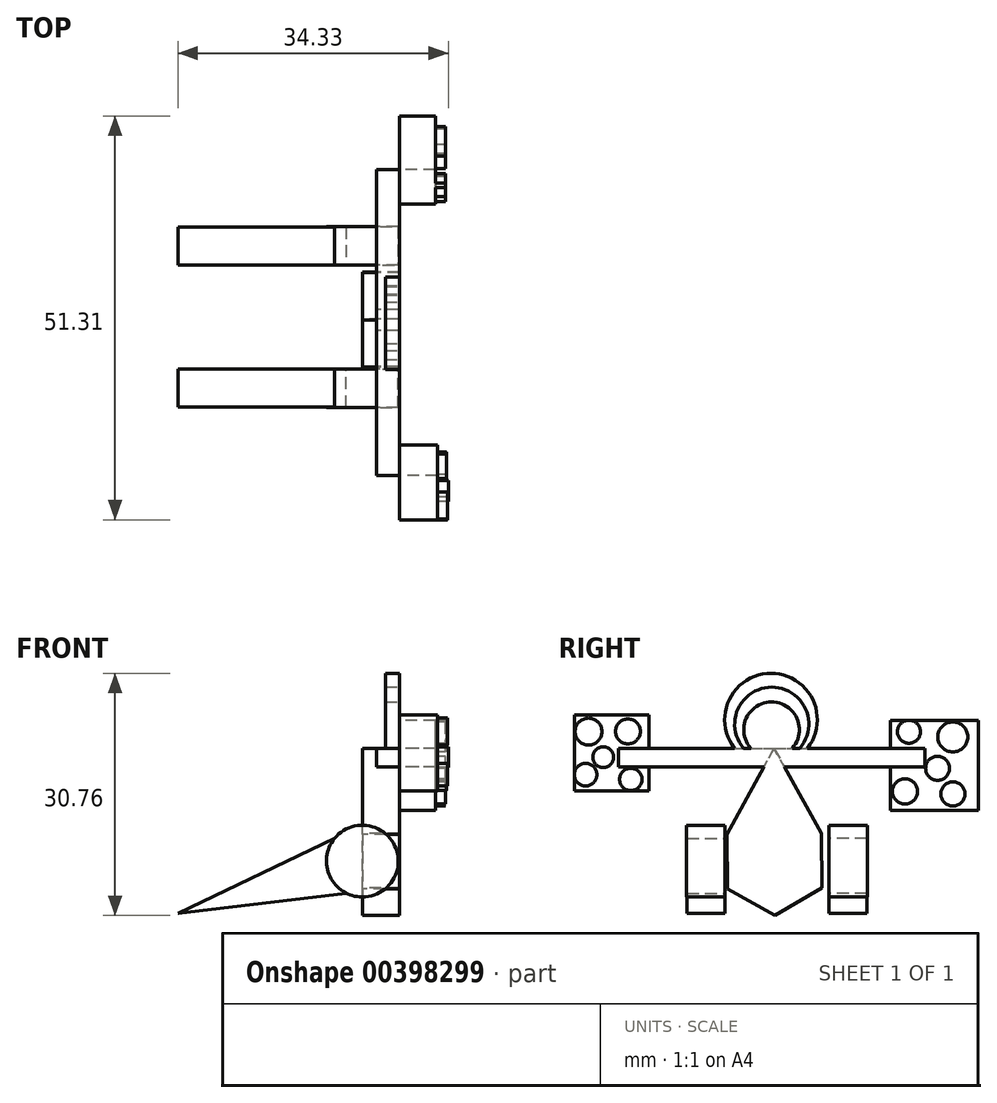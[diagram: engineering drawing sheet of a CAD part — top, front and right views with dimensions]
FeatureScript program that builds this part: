
annotation { "Feature Type Name" : "Feature", "Feature Type Description" : "" }
export const myFeature = defineFeature(function(context is Context, id is Id, definition is map)
    precondition{}
    {
        {
            var Q0;
            Q0=qCreatedBy(makeId("Front.planeOp"),FACE);
            var sketch = newSketch(context, id + "F0", { "sketchPlane" : qUnion([Q0])});
            skCircle(sketch, "E0", {"center": v(0, 0) * mm, "radius": 91.11 * mm});
            skSolve(sketch);
        }
        {
            var Q0;
            Q0=makeQuery(id+"F0.imprint","IMPRINT",FACE,{"disambiguationData":[TD([[makeQuery(id+"F0.imprint","IMPRINT",EDGE,{"derivedFrom":sQuery(id+"F0.wireOp",EDGE,"E0")}),1.0]])]});
            extrude(context, id + "F1", {"entities" : qUnion([Q0]), "depth" : 98.04 * mm});
        }
        {
            var Q0;
            Q0=makeQuery(id+"F1.opExtrude","CAP_FACE",FACE,{"disambiguationData":[OSD([sQuery(id+"F0.wireOp",EDGE,"E0")])],"isStart":true});
            var sketch = newSketch(context, id + "F2", { "sketchPlane" : qUnion([Q0])});
            skLineSegment(sketch, "E1", {"start": v(0, 91.11) * mm, "end": v(-434.23, -92.92) * mm});
            skLineSegment(sketch, "E2", {"start": v(0, -76.65) * mm, "end": v(-434.23, -92.92) * mm});
            skLineSegment(sketch, "E3", {"start": v(0, 91.11) * mm, "end": v(468.1, -132.24) * mm});
            skLineSegment(sketch, "E4", {"start": v(468.1, -132.24) * mm, "end": v(0, -76.65) * mm});
            skSolve(sketch);
        }
        {
            var Q0;
            {var subQ0=sQuery(id+"F2.wireOp",EDGE,"E4");var subQ1=sQuery(id+"F2.wireOp",EDGE,"E3");var subQ2=makeQuery(id+"F2.imprint","INTERSECT",VERTEX,{"derivedFrom":[subQ1,subQ0]});Q0=makeQuery(id+"F2.imprint","IMPRINT",FACE,{"disambiguationData":[TD([[makeQuery(id+"F2.imprint","IMPRINT",EDGE,{"disambiguationData":[TD([[subQ2,1.0]])],"derivedFrom":subQ1}),-1.0]])]});}
            extrude(context, id + "F3", {"entities" : qUnion([Q0]), "operationType" : NewBodyOperationType.ADD, "oppositeDirection" : true, "depth" : 96.52 * mm});
        }
        {
            var Q0;
            Q0=makeQuery(id+"F1.opExtrude","SWEPT_BODY",BODY,{"disambiguationData":[OSD([sQuery(id+"F0.wireOp",EDGE,"E0")])]});
            var Q1;
            Q1=qCreatedBy(makeId("Front.planeOp"),FACE);
            mirror(context, id + "F4", {"entities" : qUnion([Q0]), "mirrorPlane" : qUnion([Q1])});
        }
        {
            var Q0;
            Q0=makeQuery(id+"F4.opPattern","COPY",BODY,{"derivedFrom":makeQuery(id+"F1.opExtrude","SWEPT_BODY",BODY,{"disambiguationData":[OSD([sQuery(id+"F0.wireOp",EDGE,"E0")])]}),"instanceName":"1"});
            transform(context, id + "F5", {"entities" : qUnion([Q0]), "transformType" : TransformType.TRANSLATION_3D, "dx" : 0 * mm, "dy" : 264.16 * mm, "dz" : 0 * mm, "makeCopy" : false});
        }
        {
            var Q0;
            Q0=qCreatedBy(makeId("Right.planeOp"),FACE);
            var sketch = newSketch(context, id + "F6", { "sketchPlane" : qUnion([Q0])});
            skCircle(sketch, "E5.cCircle", {"center": v(125.72, 0) * mm, "radius": 119.75 * mm, "construction": true});
            skLineSegment(sketch, "E5.0", {"start": v(5.37, 68.07) * mm, "end": v(124.5, 138.26) * mm});
            skLineSegment(sketch, "E5.1", {"start": v(124.5, 138.26) * mm, "end": v(244.85, 70.2) * mm});
            skLineSegment(sketch, "E5.2", {"start": v(244.85, 70.2) * mm, "end": v(246.08, -68.07) * mm});
            skLineSegment(sketch, "E5.3", {"start": v(246.08, -68.07) * mm, "end": v(126.95, -138.26) * mm});
            skLineSegment(sketch, "E5.4", {"start": v(126.95, -138.26) * mm, "end": v(6.6, -70.2) * mm});
            skLineSegment(sketch, "E5.5", {"start": v(6.6, -70.2) * mm, "end": v(5.37, 68.07) * mm});
            skPoint(sketch, "E5.0.midPoint", {"position": v(64.93, 103.17) * mm});
            skSolve(sketch);
        }
        {
            var Q0;
            Q0=makeQuery(id+"F6.imprint","IMPRINT",FACE,{"disambiguationData":[TD([[makeQuery(id+"F6.imprint","IMPRINT",EDGE,{"derivedFrom":sQuery(id+"F6.wireOp",EDGE,"E5.0")}),-1.0]])]});
            extrude(context, id + "F7", {"entities" : qUnion([Q0]), "depth" : 93.98 * mm});
        }
        {
            var Q0;
            Q0=makeQuery(id+"F7.opExtrude","CAP_FACE",FACE,{"disambiguationData":[OSD([sQuery(id+"F6.wireOp",EDGE,"E5.0"),sQuery(id+"F6.wireOp",EDGE,"E5.1"),sQuery(id+"F6.wireOp",EDGE,"E5.2"),sQuery(id+"F6.wireOp",EDGE,"E5.3"),sQuery(id+"F6.wireOp",EDGE,"E5.4"),sQuery(id+"F6.wireOp",EDGE,"E5.5")])],"isStart":false});
            var sketch = newSketch(context, id + "F8", { "sketchPlane" : qUnion([Q0])});
            skLineSegment(sketch, "E6", {"start": v(5.37, 68.07) * mm, "end": v(124.5, 286.89) * mm});
            skLineSegment(sketch, "E7", {"start": v(244.85, 70.2) * mm, "end": v(124.5, 286.89) * mm});
            skSolve(sketch);
        }
        {
            var Q0;
            Q0=makeQuery(id+"F8.imprint","IMPRINT",FACE,{"disambiguationData":[TD([[makeQuery(id+"F8.imprint","IMPRINT",EDGE,{"derivedFrom":sQuery(id+"F8.wireOp",EDGE,"E6")}),-1.0]])]});
            extrude(context, id + "F9", {"entities" : qUnion([Q0]), "operationType" : NewBodyOperationType.ADD, "oppositeDirection" : true, "depth" : 93.98 * mm});
        }
        {
            var Q0;
            {var subQ0=sQuery(id+"F6.wireOp",EDGE,"E5.1");var subQ1=sQuery(id+"F6.wireOp",EDGE,"E5.0");Q0=makeQuery(id+"F9.boolean.opBoolean","MERGE",FACE,{"derivedFrom":[makeQuery(id+"F7.opExtrude","CAP_FACE",FACE,{"disambiguationData":[OSD([subQ1,subQ0,sQuery(id+"F6.wireOp",EDGE,"E5.2"),sQuery(id+"F6.wireOp",EDGE,"E5.3"),sQuery(id+"F6.wireOp",EDGE,"E5.4"),sQuery(id+"F6.wireOp",EDGE,"E5.5")])],"isStart":false}),makeQuery(id+"F9.opExtrude","CAP_FACE",FACE,{"disambiguationData":[OSD([subQ1,subQ0,sQuery(id+"F8.wireOp",EDGE,"E6"),sQuery(id+"F8.wireOp",EDGE,"E7")])],"isStart":true})]});}
            var sketch = newSketch(context, id + "F10", { "sketchPlane" : qUnion([Q0])});
            skLineSegment(sketch, "E8.bottom", {"start": v(-270.15, 286.89) * mm, "end": v(507.6, 286.89) * mm});
            skLineSegment(sketch, "E8.top", {"start": v(-270.15, 238.84) * mm, "end": v(507.6, 238.84) * mm});
            skLineSegment(sketch, "E8.left", {"start": v(-270.15, 286.89) * mm, "end": v(-270.15, 238.84) * mm});
            skLineSegment(sketch, "E8.right", {"start": v(507.6, 286.89) * mm, "end": v(507.6, 238.84) * mm});
            skSolve(sketch);
        }
        {
            var Q0;
            Q0 = qSketchRegion(id + "F10", true);
            extrude(context, id + "F11", {"entities" : qUnion([Q0]), "operationType" : NewBodyOperationType.ADD, "oppositeDirection" : true, "depth" : 58.42 * mm});
        }
        {
            var Q0;
            {var subQ0=sQuery(id+"F6.wireOp",EDGE,"E5.1");var subQ1=sQuery(id+"F6.wireOp",EDGE,"E5.0");Q0=makeQuery(id+"F11.boolean.opBoolean","MERGE",FACE,{"derivedFrom":[makeQuery(id+"F9.boolean.opBoolean","MERGE",FACE,{"derivedFrom":[makeQuery(id+"F7.opExtrude","CAP_FACE",FACE,{"disambiguationData":[OSD([subQ1,subQ0,sQuery(id+"F6.wireOp",EDGE,"E5.2"),sQuery(id+"F6.wireOp",EDGE,"E5.3"),sQuery(id+"F6.wireOp",EDGE,"E5.4"),sQuery(id+"F6.wireOp",EDGE,"E5.5")])],"isStart":false}),makeQuery(id+"F9.opExtrude","CAP_FACE",FACE,{"disambiguationData":[OSD([subQ1,subQ0,sQuery(id+"F8.wireOp",EDGE,"E6"),sQuery(id+"F8.wireOp",EDGE,"E7")])],"isStart":true})]}),makeQuery(id+"F11.opExtrude","CAP_FACE",FACE,{"disambiguationData":[OSD([sQuery(id+"F10.wireOp",EDGE,"E8.bottom"),sQuery(id+"F10.wireOp",EDGE,"E8.top"),sQuery(id+"F10.wireOp",EDGE,"E8.left"),sQuery(id+"F10.wireOp",EDGE,"E8.right")])],"isStart":true})]});}
            var sketch = newSketch(context, id + "F12", { "sketchPlane" : qUnion([Q0])});
            skLineSegment(sketch, "E9.bottom", {"start": v(-383, 179.03) * mm, "end": v(-193.33, 179.03) * mm});
            skLineSegment(sketch, "E9.top", {"start": v(-383, 371.33) * mm, "end": v(-193.33, 371.33) * mm});
            skLineSegment(sketch, "E9.left", {"start": v(-383, 179.03) * mm, "end": v(-383, 371.33) * mm});
            skLineSegment(sketch, "E9.right", {"start": v(-193.33, 179.03) * mm, "end": v(-193.33, 371.33) * mm});
            skSolve(sketch);
        }
        {
            var Q0;
            {var subQ1=sQuery(id+"F12.wireOp",EDGE,"E9.bottom");Q0=makeQuery(id+"F12.imprint","IMPRINT",FACE,{"disambiguationData":[TD([[makeQuery(id+"F12.imprint","IMPRINT",EDGE,{"derivedFrom":subQ1}),1.0]])]});}
            extrude(context, id + "F13", {"entities" : qUnion([Q0]), "depth" : 96.52 * mm});
        }
        {
            var Q0;
            {var subQ0=sQuery(id+"F6.wireOp",EDGE,"E5.1");var subQ1=sQuery(id+"F6.wireOp",EDGE,"E5.0");Q0=makeQuery(id+"F11.boolean.opBoolean","MERGE",FACE,{"derivedFrom":[makeQuery(id+"F9.boolean.opBoolean","MERGE",FACE,{"derivedFrom":[makeQuery(id+"F7.opExtrude","CAP_FACE",FACE,{"disambiguationData":[OSD([subQ1,subQ0,sQuery(id+"F6.wireOp",EDGE,"E5.2"),sQuery(id+"F6.wireOp",EDGE,"E5.3"),sQuery(id+"F6.wireOp",EDGE,"E5.4"),sQuery(id+"F6.wireOp",EDGE,"E5.5")])],"isStart":false}),makeQuery(id+"F9.opExtrude","CAP_FACE",FACE,{"disambiguationData":[OSD([subQ1,subQ0,sQuery(id+"F8.wireOp",EDGE,"E6"),sQuery(id+"F8.wireOp",EDGE,"E7")])],"isStart":true})]}),makeQuery(id+"F11.opExtrude","CAP_FACE",FACE,{"disambiguationData":[OSD([sQuery(id+"F10.wireOp",EDGE,"E8.bottom"),sQuery(id+"F10.wireOp",EDGE,"E8.top"),sQuery(id+"F10.wireOp",EDGE,"E8.left"),sQuery(id+"F10.wireOp",EDGE,"E8.right")])],"isStart":true})]});}
            var sketch = newSketch(context, id + "F14", { "sketchPlane" : qUnion([Q0])});
            skLineSegment(sketch, "E10.bottom", {"start": v(643.3, 129.12) * mm, "end": v(420.02, 129.12) * mm});
            skLineSegment(sketch, "E10.top", {"start": v(643.3, 357.33) * mm, "end": v(420.02, 357.33) * mm});
            skLineSegment(sketch, "E10.left", {"start": v(643.3, 129.12) * mm, "end": v(643.3, 357.33) * mm});
            skLineSegment(sketch, "E10.right", {"start": v(420.02, 129.12) * mm, "end": v(420.02, 357.33) * mm});
            skSolve(sketch);
        }
        {
            var Q0;
            {var subQ1=sQuery(id+"F14.wireOp",EDGE,"E10.bottom");Q0=makeQuery(id+"F14.imprint","IMPRINT",FACE,{"disambiguationData":[TD([[makeQuery(id+"F14.imprint","IMPRINT",EDGE,{"derivedFrom":subQ1}),-1.0]])]});}
            extrude(context, id + "F15", {"entities" : qUnion([Q0]), "depth" : 91.44 * mm});
        }
        {
            var Q0;
            Q0=makeQuery(id+"F13.opExtrude","CAP_FACE",FACE,{"disambiguationData":[OSD([sQuery(id+"F10.wireOp",EDGE,"E8.bottom"),sQuery(id+"F10.wireOp",EDGE,"E8.top"),sQuery(id+"F10.wireOp",EDGE,"E8.left"),sQuery(id+"F12.wireOp",EDGE,"E9.bottom"),sQuery(id+"F12.wireOp",EDGE,"E9.top"),sQuery(id+"F12.wireOp",EDGE,"E9.left"),sQuery(id+"F12.wireOp",EDGE,"E9.right")])],"isStart":false});
            var sketch = newSketch(context, id + "F16", { "sketchPlane" : qUnion([Q0])});
            skCircle(sketch, "E11", {"center": v(-239.34, 329.1) * mm, "radius": 32.95 * mm});
            skPoint(sketch, "E11.centerSnap0", {"position": v(-193.33, 329.1) * mm});
            skCircle(sketch, "E12", {"center": v(-346.66, 329.1) * mm, "radius": 34.15 * mm});
            skCircle(sketch, "E13", {"center": v(-354.15, 219.75) * mm, "radius": 28.7 * mm});
            skCircle(sketch, "E14", {"center": v(-239.34, 207.67) * mm, "radius": 28.52 * mm});
            skCircle(sketch, "E15", {"center": v(-309.5, 263.98) * mm, "radius": 26.29 * mm});
            skSolve(sketch);
        }
        {
            var Q0;
            Q0=makeQuery(id+"F16.imprint","IMPRINT",FACE,{"disambiguationData":[TD([[makeQuery(id+"F16.imprint","IMPRINT",EDGE,{"derivedFrom":sQuery(id+"F16.wireOp",EDGE,"E12")}),1.0]])]});
            var Q1;
            Q1=sQuery(id+"F16.wireOp",EDGE,"E12");
            extrude(context, id + "F17", {"entities" : qUnion([Q0]), "operationType" : NewBodyOperationType.ADD, "surfaceEntities" : qUnion([Q1]), "depth" : 25.4 * mm});
        }
        {
            var Q0;
            Q0=makeQuery(id+"F13.opExtrude","CAP_FACE",FACE,{"disambiguationData":[OSD([sQuery(id+"F10.wireOp",EDGE,"E8.bottom"),sQuery(id+"F10.wireOp",EDGE,"E8.top"),sQuery(id+"F10.wireOp",EDGE,"E8.left"),sQuery(id+"F12.wireOp",EDGE,"E9.bottom"),sQuery(id+"F12.wireOp",EDGE,"E9.top"),sQuery(id+"F12.wireOp",EDGE,"E9.left"),sQuery(id+"F12.wireOp",EDGE,"E9.right")])],"isStart":false});
            var sketch = newSketch(context, id + "F18", { "sketchPlane" : qUnion([Q0])});
            skCircle(sketch, "E16", {"center": v(-246.53, 329.52) * mm, "radius": 31.43 * mm});
            skSolve(sketch);
        }
        {
            var Q0;
            Q0=makeQuery(id+"F18.imprint","IMPRINT",FACE,{"disambiguationData":[TD([[makeQuery(id+"F18.imprint","IMPRINT",EDGE,{"derivedFrom":sQuery(id+"F18.wireOp",EDGE,"E16")}),1.0]])]});
            var Q1;
            Q1=sQuery(id+"F18.wireOp",EDGE,"E16");
            extrude(context, id + "F19", {"entities" : qUnion([Q0]), "operationType" : NewBodyOperationType.ADD, "surfaceEntities" : qUnion([Q1]), "endBound" : BoundingType.SYMMETRIC, "depth" : 45.72 * mm});
        }
        {
            var Q0;
            Q0=makeQuery(id+"F16.imprint","IMPRINT",FACE,{"disambiguationData":[TD([[makeQuery(id+"F16.imprint","IMPRINT",EDGE,{"derivedFrom":sQuery(id+"F16.wireOp",EDGE,"E15")}),1.0]])]});
            var Q1;
            Q1=sQuery(id+"F16.wireOp",EDGE,"E15");
            extrude(context, id + "F20", {"entities" : qUnion([Q0]), "operationType" : NewBodyOperationType.ADD, "surfaceEntities" : qUnion([Q1]), "depth" : 27.94 * mm});
        }
        {
            var Q0;
            Q0=makeQuery(id+"F16.imprint","IMPRINT",FACE,{"disambiguationData":[TD([[makeQuery(id+"F16.imprint","IMPRINT",EDGE,{"derivedFrom":sQuery(id+"F16.wireOp",EDGE,"E13")}),1.0]])]});
            var Q1;
            Q1=sQuery(id+"F16.wireOp",EDGE,"E13");
            extrude(context, id + "F21", {"entities" : qUnion([Q0]), "operationType" : NewBodyOperationType.ADD, "surfaceEntities" : qUnion([Q1]), "depth" : 25.4 * mm});
        }
        {
            var Q0;
            Q0=makeQuery(id+"F16.imprint","IMPRINT",FACE,{"disambiguationData":[TD([[makeQuery(id+"F16.imprint","IMPRINT",EDGE,{"derivedFrom":sQuery(id+"F16.wireOp",EDGE,"E14")}),1.0]])]});
            var Q1;
            Q1=sQuery(id+"F16.wireOp",EDGE,"E14");
            extrude(context, id + "F22", {"entities" : qUnion([Q0]), "operationType" : NewBodyOperationType.ADD, "surfaceEntities" : qUnion([Q1]), "depth" : 22.86 * mm});
        }
        {
            var Q0;
            Q0=makeQuery(id+"F15.opExtrude","CAP_FACE",FACE,{"disambiguationData":[OSD([sQuery(id+"F10.wireOp",EDGE,"E8.bottom"),sQuery(id+"F10.wireOp",EDGE,"E8.top"),sQuery(id+"F10.wireOp",EDGE,"E8.right"),sQuery(id+"F14.wireOp",EDGE,"E10.bottom"),sQuery(id+"F14.wireOp",EDGE,"E10.top"),sQuery(id+"F14.wireOp",EDGE,"E10.left"),sQuery(id+"F14.wireOp",EDGE,"E10.right")])],"isStart":false});
            var sketch = newSketch(context, id + "F23", { "sketchPlane" : qUnion([Q0])});
            skCircle(sketch, "E17", {"center": v(578.72, 315.62) * mm, "radius": 38.04 * mm});
            skCircle(sketch, "E18", {"center": v(457.24, 177.07) * mm, "radius": 32 * mm});
            skCircle(sketch, "E19", {"center": v(579.03, 170.7) * mm, "radius": 30.77 * mm});
            skCircle(sketch, "E20", {"center": v(467.35, 328.58) * mm, "radius": 29.36 * mm});
            skCircle(sketch, "E21", {"center": v(540.02, 235.78) * mm, "radius": 30.37 * mm});
            skSolve(sketch);
        }
        {
            var Q0;
            {var subQ0=sQuery(id+"F23.wireOp",EDGE,"E20");var subQ1=makeQuery(id+"F15.opExtrude","CAP_EDGE",EDGE,{"disambiguationData":[OSD([sQuery(id+"F14.wireOp",EDGE,"E10.top")])],"isStart":false});var subQ2=makeQuery(id+"F23.imprint","INTERSECT",VERTEX,{"disambiguationData":[OD(0.0)],"derivedFrom":[subQ1,subQ0]});Q0=makeQuery(id+"F23.imprint","IMPRINT",FACE,{"disambiguationData":[TD([[makeQuery(id+"F23.imprint","IMPRINT",EDGE,{"disambiguationData":[TD([[subQ2,1.0]])],"derivedFrom":subQ0}),1.0]])]});}
            var Q1;
            Q1=sQuery(id+"F23.wireOp",EDGE,"E20");
            extrude(context, id + "F24", {"entities" : qUnion([Q0]), "operationType" : NewBodyOperationType.ADD, "surfaceEntities" : qUnion([Q1]), "depth" : 25.4 * mm});
        }
        {
            var Q0;
            Q0=makeQuery(id+"F23.imprint","IMPRINT",FACE,{"disambiguationData":[TD([[makeQuery(id+"F23.imprint","IMPRINT",EDGE,{"derivedFrom":sQuery(id+"F23.wireOp",EDGE,"E17")}),1.0]])]});
            var Q1;
            Q1=sQuery(id+"F23.wireOp",EDGE,"E17");
            extrude(context, id + "F25", {"entities" : qUnion([Q0]), "operationType" : NewBodyOperationType.ADD, "surfaceEntities" : qUnion([Q1]), "depth" : 25.4 * mm});
        }
        {
            var Q0;
            Q0=makeQuery(id+"F23.imprint","IMPRINT",FACE,{"disambiguationData":[TD([[makeQuery(id+"F23.imprint","IMPRINT",EDGE,{"derivedFrom":sQuery(id+"F23.wireOp",EDGE,"E21")}),1.0]])]});
            var Q1;
            Q1=sQuery(id+"F23.wireOp",EDGE,"E21");
            extrude(context, id + "F26", {"entities" : qUnion([Q0]), "operationType" : NewBodyOperationType.ADD, "surfaceEntities" : qUnion([Q1]), "depth" : 25.4 * mm});
        }
        {
            var Q0;
            Q0=makeQuery(id+"F23.imprint","IMPRINT",FACE,{"disambiguationData":[TD([[makeQuery(id+"F23.imprint","IMPRINT",EDGE,{"derivedFrom":sQuery(id+"F23.wireOp",EDGE,"E18")}),1.0]])]});
            var Q1;
            Q1=sQuery(id+"F23.wireOp",EDGE,"E18");
            extrude(context, id + "F27", {"entities" : qUnion([Q0]), "operationType" : NewBodyOperationType.ADD, "surfaceEntities" : qUnion([Q1]), "depth" : 25.4 * mm});
        }
        {
            var Q0;
            Q0=makeQuery(id+"F23.imprint","IMPRINT",FACE,{"disambiguationData":[TD([[makeQuery(id+"F23.imprint","IMPRINT",EDGE,{"derivedFrom":sQuery(id+"F23.wireOp",EDGE,"E19")}),1.0]])]});
            extrude(context, id + "F28", {"entities" : qUnion([Q0]), "operationType" : NewBodyOperationType.ADD, "depth" : 25.4 * mm});
        }
        {
            var Q0;
            {var subQ0=sQuery(id+"F6.wireOp",EDGE,"E5.1");var subQ1=sQuery(id+"F6.wireOp",EDGE,"E5.0");Q0=makeQuery(id+"F11.boolean.opBoolean","MERGE",FACE,{"derivedFrom":[makeQuery(id+"F9.boolean.opBoolean","MERGE",FACE,{"derivedFrom":[makeQuery(id+"F7.opExtrude","CAP_FACE",FACE,{"disambiguationData":[OSD([subQ1,subQ0,sQuery(id+"F6.wireOp",EDGE,"E5.2"),sQuery(id+"F6.wireOp",EDGE,"E5.3"),sQuery(id+"F6.wireOp",EDGE,"E5.4"),sQuery(id+"F6.wireOp",EDGE,"E5.5")])],"isStart":false}),makeQuery(id+"F9.opExtrude","CAP_FACE",FACE,{"disambiguationData":[OSD([subQ1,subQ0,sQuery(id+"F8.wireOp",EDGE,"E6"),sQuery(id+"F8.wireOp",EDGE,"E7")])],"isStart":true})]}),makeQuery(id+"F11.opExtrude","CAP_FACE",FACE,{"disambiguationData":[OSD([sQuery(id+"F10.wireOp",EDGE,"E8.bottom"),sQuery(id+"F10.wireOp",EDGE,"E8.top"),sQuery(id+"F10.wireOp",EDGE,"E8.left"),sQuery(id+"F10.wireOp",EDGE,"E8.right")])],"isStart":true})]});}
            var sketch = newSketch(context, id + "F29", { "sketchPlane" : qUnion([Q0])});
            skArc(sketch, "E22", {"start": v(233.56, 286.89) * mm, "mid": v(116.78, 510.28) * mm, "end": v(0, 286.89) * mm});
            skSolve(sketch);
        }
        {
            var Q0;
            Q0=sQuery(id+"F29.wireOp",EDGE,"E22");
            extrude(context, id + "F30", {"bodyType" : ToolBodyType.SURFACE, "surfaceEntities" : qUnion([Q0]), "oppositeDirection" : true, "depth" : 55.88 * mm});
        }
        {
            var Q0;
            {var subQ0=sQuery(id+"F6.wireOp",EDGE,"E5.1");var subQ1=sQuery(id+"F6.wireOp",EDGE,"E5.0");Q0=makeQuery(id+"F11.boolean.opBoolean","MERGE",FACE,{"derivedFrom":[makeQuery(id+"F9.boolean.opBoolean","MERGE",FACE,{"derivedFrom":[makeQuery(id+"F7.opExtrude","CAP_FACE",FACE,{"disambiguationData":[OSD([subQ1,subQ0,sQuery(id+"F6.wireOp",EDGE,"E5.2"),sQuery(id+"F6.wireOp",EDGE,"E5.3"),sQuery(id+"F6.wireOp",EDGE,"E5.4"),sQuery(id+"F6.wireOp",EDGE,"E5.5")])],"isStart":false}),makeQuery(id+"F9.opExtrude","CAP_FACE",FACE,{"disambiguationData":[OSD([subQ1,subQ0,sQuery(id+"F8.wireOp",EDGE,"E6"),sQuery(id+"F8.wireOp",EDGE,"E7")])],"isStart":true})]}),makeQuery(id+"F11.opExtrude","CAP_FACE",FACE,{"disambiguationData":[OSD([sQuery(id+"F10.wireOp",EDGE,"E8.bottom"),sQuery(id+"F10.wireOp",EDGE,"E8.top"),sQuery(id+"F10.wireOp",EDGE,"E8.left"),sQuery(id+"F10.wireOp",EDGE,"E8.right")])],"isStart":true})]});}
            var sketch = newSketch(context, id + "F31", { "sketchPlane" : qUnion([Q0])});
            skArc(sketch, "E23", {"start": v(209.6, 286.89) * mm, "mid": v(116.89, 477.07) * mm, "end": v(24.18, 286.89) * mm});
            skArc(sketch, "E24", {"start": v(190.35, 286.89) * mm, "mid": v(118.69, 441.99) * mm, "end": v(47.02, 286.89) * mm});
            skArc(sketch, "E25", {"start": v(170.94, 286.89) * mm, "mid": v(118.21, 404.41) * mm, "end": v(65.48, 286.89) * mm});
            skArc(sketch, "E26", {"start": v(147.33, 286.89) * mm, "mid": v(117.05, 359.38) * mm, "end": v(86.77, 286.89) * mm});
            skSolve(sketch);
        }
        {
            var Q0;
            {var subQ0=sQuery(id+"F31.wireOp",EDGE,"E23");Q0=makeQuery(id+"F31.imprint","IMPRINT",FACE,{"disambiguationData":[TD([[makeQuery(id+"F31.imprint","IMPRINT",EDGE,{"derivedFrom":subQ0}),1.0]])]});}
            var Q1;
            {var subQ0=sQuery(id+"F31.wireOp",EDGE,"E26");Q1=makeQuery(id+"F31.imprint","IMPRINT",FACE,{"disambiguationData":[TD([[makeQuery(id+"F31.imprint","IMPRINT",EDGE,{"derivedFrom":subQ0}),1.0]])]});}
            var Q2;
            {var subQ0=sQuery(id+"F31.wireOp",EDGE,"E25");Q2=makeQuery(id+"F31.imprint","IMPRINT",FACE,{"disambiguationData":[TD([[makeQuery(id+"F31.imprint","IMPRINT",EDGE,{"derivedFrom":subQ0}),1.0]])]});}
            extrude(context, id + "F32", {"entities" : qUnion([Q0, Q1, Q2]), "operationType" : NewBodyOperationType.ADD, "oppositeDirection" : true, "depth" : 35.56 * mm});
        }
        {
            var Q0;
            Q0=makeQuery(id+"F7.opExtrude","SWEPT_BODY",BODY,{"disambiguationData":[OSD([sQuery(id+"F6.wireOp",EDGE,"E5.0"),sQuery(id+"F6.wireOp",EDGE,"E5.1"),sQuery(id+"F6.wireOp",EDGE,"E5.2"),sQuery(id+"F6.wireOp",EDGE,"E5.3"),sQuery(id+"F6.wireOp",EDGE,"E5.4"),sQuery(id+"F6.wireOp",EDGE,"E5.5")])]});
            var Q1;
            Q1=makeQuery(id+"F13.opExtrude","SWEPT_BODY",BODY,{"disambiguationData":[OSD([sQuery(id+"F10.wireOp",EDGE,"E8.bottom"),sQuery(id+"F10.wireOp",EDGE,"E8.top"),sQuery(id+"F10.wireOp",EDGE,"E8.left"),sQuery(id+"F12.wireOp",EDGE,"E9.bottom"),sQuery(id+"F12.wireOp",EDGE,"E9.top"),sQuery(id+"F12.wireOp",EDGE,"E9.left"),sQuery(id+"F12.wireOp",EDGE,"E9.right")])]});
            var Q2;
            Q2=makeQuery(id+"F15.opExtrude","SWEPT_BODY",BODY,{"disambiguationData":[OSD([sQuery(id+"F10.wireOp",EDGE,"E8.bottom"),sQuery(id+"F10.wireOp",EDGE,"E8.top"),sQuery(id+"F10.wireOp",EDGE,"E8.right"),sQuery(id+"F14.wireOp",EDGE,"E10.bottom"),sQuery(id+"F14.wireOp",EDGE,"E10.top"),sQuery(id+"F14.wireOp",EDGE,"E10.left"),sQuery(id+"F14.wireOp",EDGE,"E10.right")])]});
            var Q3;
            Q3=makeQuery(id+"F30.opExtrude","SWEPT_BODY",BODY,{"disambiguationData":[OSD([sQuery(id+"F29.wireOp",EDGE,"E22")])]});
            var Q4;
            Q4=makeQuery(id+"F4.opPattern","COPY",BODY,{"derivedFrom":makeQuery(id+"F1.opExtrude","SWEPT_BODY",BODY,{"disambiguationData":[OSD([sQuery(id+"F0.wireOp",EDGE,"E0")])]}),"instanceName":"1"});
            var Q5;
            Q5=makeQuery(id+"F1.opExtrude","SWEPT_BODY",BODY,{"disambiguationData":[OSD([sQuery(id+"F0.wireOp",EDGE,"E0")])]});
            var Q6;
            Q6=qCreatedBy(makeId("Origin.pointOp"),VERTEX);
            transform(context, id + "F33", {"entities" : qUnion([Q0, Q1, Q2, Q3, Q4, Q5]), "transformType" : TransformType.SCALE_UNIFORMLY, "scale" : 2 / 40, "scalePoint" : qUnion([Q6]), "makeCopy" : false});
        }
    });
